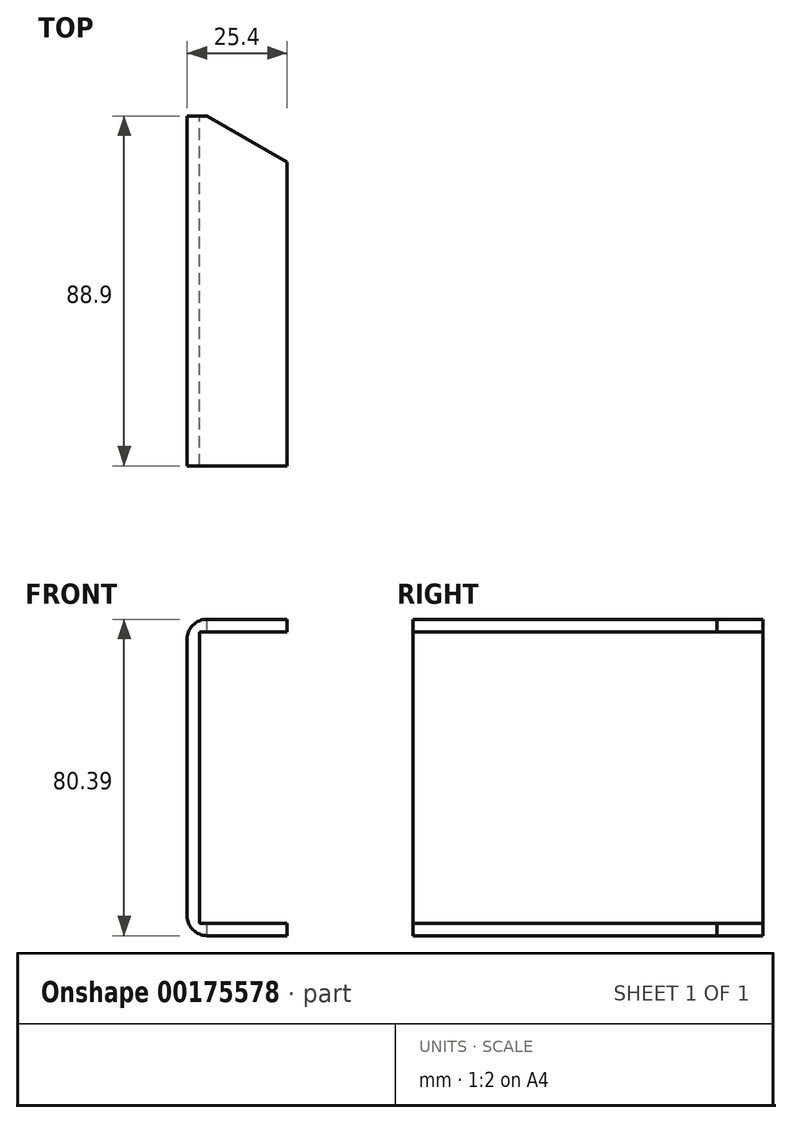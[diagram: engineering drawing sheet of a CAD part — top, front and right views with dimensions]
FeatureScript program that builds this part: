
annotation { "Feature Type Name" : "Feature", "Feature Type Description" : "" }
export const myFeature = defineFeature(function(context is Context, id is Id, definition is map)
    precondition{}
    {
        {
            var Q0;
            Q0=qCreatedBy(makeId("Front.planeOp"),FACE);
            var sketch = newSketch(context, id + "F0", { "sketchPlane" : qUnion([Q0])});
            skLineSegment(sketch, "E0", {"start": v(6.6, 68.07) * mm, "end": v(-18.8, 68.07) * mm});
            skLineSegment(sketch, "E1", {"start": v(-18.8, 68.07) * mm, "end": v(-18.8, -12.32) * mm});
            skLineSegment(sketch, "E2", {"start": v(-18.8, -12.32) * mm, "end": v(6.6, -12.32) * mm});
            skLineSegment(sketch, "E3", {"start": v(6.6, -12.32) * mm, "end": v(6.6, -9.15) * mm});
            skLineSegment(sketch, "E4", {"start": v(6.6, -9.15) * mm, "end": v(-15.63, -9.15) * mm});
            skLineSegment(sketch, "E5", {"start": v(-15.63, -9.15) * mm, "end": v(-15.63, 64.9) * mm});
            skLineSegment(sketch, "E6", {"start": v(-15.63, 64.9) * mm, "end": v(6.6, 64.9) * mm});
            skLineSegment(sketch, "E7", {"start": v(6.6, 64.9) * mm, "end": v(6.6, 68.07) * mm});
            skSolve(sketch);
        }
        {
            var Q0;
            Q0 = qSketchRegion(id + "F0", true);
            extrude(context, id + "F1", {"entities" : qUnion([Q0]), "depth" : 88.9 * mm});
        }
        {
            var Q0;
            Q0=makeQuery(id+"F1.opExtrude","SWEPT_EDGE",EDGE,{"disambiguationData":[OSD([sQuery(id+"F0.wireOp",EDGE,"E0"),sQuery(id+"F0.wireOp",EDGE,"E1")])]});
            var Q1;
            Q1=makeQuery(id+"F1.opExtrude","SWEPT_EDGE",EDGE,{"disambiguationData":[OSD([sQuery(id+"F0.wireOp",EDGE,"E1"),sQuery(id+"F0.wireOp",EDGE,"E2")])]});
            fillet(context, id + "F2", {"entities" : qUnion([Q0, Q1]), "radius" : 5.08 * mm, "tangentPropagation" : true, "allowEdgeOverflow" : false});
        }
        {
            var Q0;
            Q0=makeQuery(id+"F1.opExtrude","SWEPT_FACE",FACE,{"disambiguationData":[OSD([sQuery(id+"F0.wireOp",EDGE,"E0")])]});
            var sketch = newSketch(context, id + "F3", { "sketchPlane" : qUnion([Q0])});
            skLineSegment(sketch, "E8", {"start": v(-13.73, 0) * mm, "end": v(6.6, -11.73) * mm});
            skSolve(sketch);
        }
        {
            var Q0;
            {var subQ0=sQuery(id+"F3.wireOp",EDGE,"E8");Q0=makeQuery(id+"F3.imprint","IMPRINT",FACE,{"disambiguationData":[TD([[makeQuery(id+"F3.imprint","IMPRINT",EDGE,{"derivedFrom":subQ0}),1.0]])]});}
            extrude(context, id + "F4", {"entities" : qUnion([Q0]), "operationType" : NewBodyOperationType.REMOVE, "oppositeDirection" : true, "depth" : 103.38 * mm});
        }
    });
